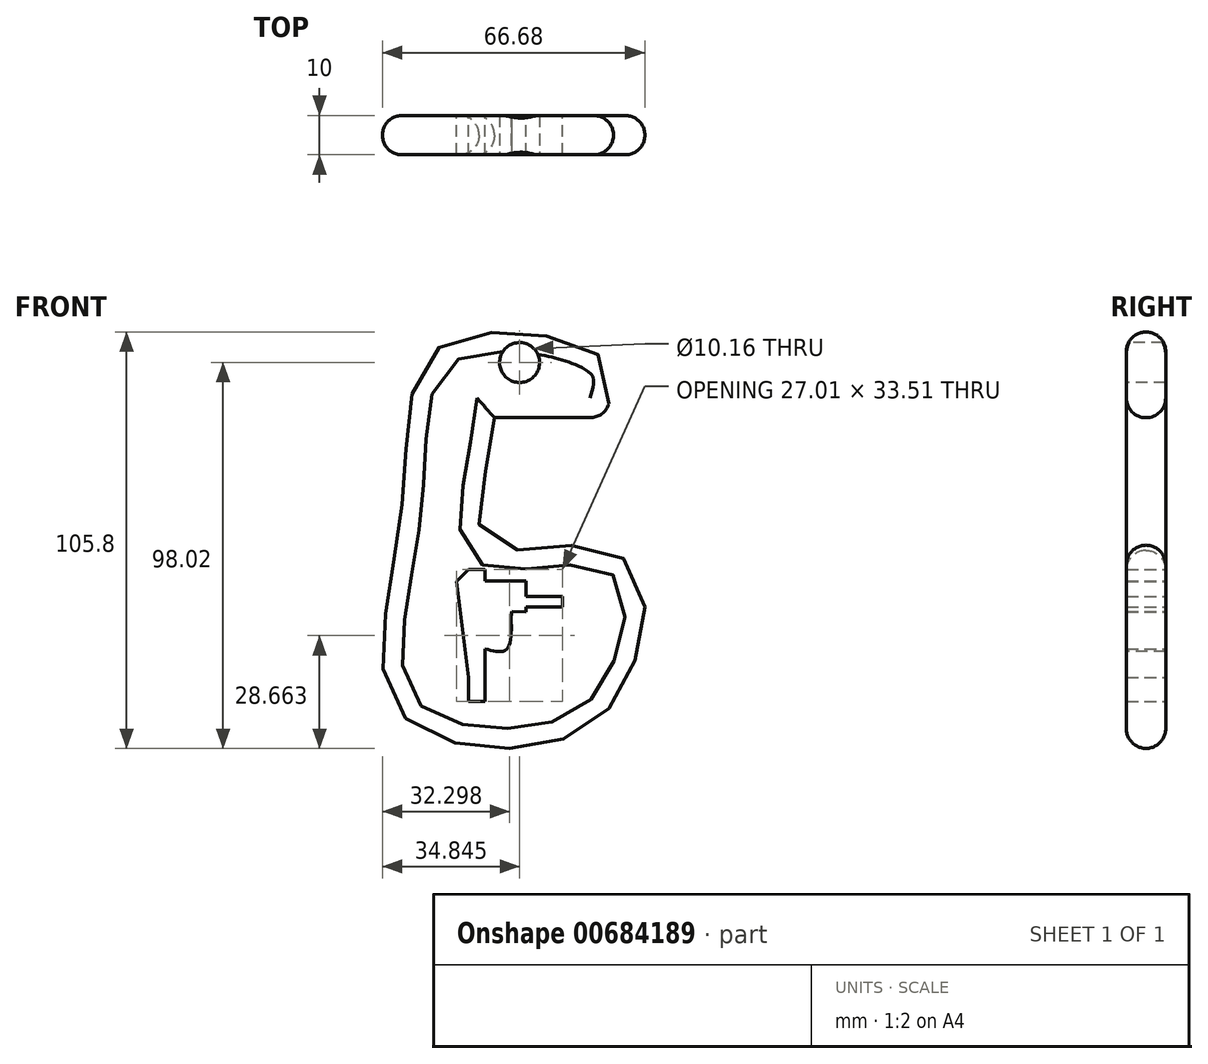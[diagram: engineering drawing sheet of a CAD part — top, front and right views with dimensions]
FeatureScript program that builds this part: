
annotation { "Feature Type Name" : "Feature", "Feature Type Description" : "" }
export const myFeature = defineFeature(function(context is Context, id is Id, definition is map)
    precondition{}
    {
        {
            var Q0;
            Q0=qCreatedBy(makeId("Front.planeOp"),FACE);
            var sketch = newSketch(context, id + "F0", { "sketchPlane" : qUnion([Q0])});
            skLineSegment(sketch, "E0", {"start": v(0, 32.39) * mm, "end": v(27.92, 32.39) * mm});
            skFitSpline(sketch, "E1", {"points": [v(27.92, 32.39) * mm, v(27.92, 47.21) * mm, v(-13.1, 50.87) * mm, v(-23.45, 9.85) * mm, v(-24.47, -41.93) * mm, v(15.74, -49.85) * mm, v(34.62, -32.19) * mm, v(36.65, -7.82) * mm, v(20.61, 0) * mm, v(-1.73, 0) * mm, v(0, 32.39) * mm], "startDerivative": vector(85.73, 266.25) * mm, "endDerivative": vector(64.37, 478.6) * mm});
            skLineSegment(sketch, "E2", {"start": v(8.02, -16.96) * mm, "end": v(8.02, -9.04) * mm});
            skLineSegment(sketch, "E3", {"start": v(8.02, -9.04) * mm, "end": v(-2.34, -9.04) * mm});
            skLineSegment(sketch, "E4", {"start": v(-2.34, -9.04) * mm, "end": v(-2.34, -6.2) * mm});
            skLineSegment(sketch, "E5", {"start": v(-2.34, -6.2) * mm, "end": v(-6.6, -6.2) * mm});
            skLineSegment(sketch, "E6", {"start": v(-6.6, -6.2) * mm, "end": v(-6.6, -39.7) * mm});
            skLineSegment(sketch, "E7", {"start": v(-6.6, -39.7) * mm, "end": v(-2.34, -39.7) * mm});
            skLineSegment(sketch, "E8", {"start": v(-2.34, -39.7) * mm, "end": v(-2.34, -16.55) * mm});
            skLineSegment(sketch, "E9", {"start": v(-2.34, -16.55) * mm, "end": v(8.02, -16.96) * mm});
            skLineSegment(sketch, "E10", {"start": v(8.02, -13) * mm, "end": v(17.36, -13) * mm});
            skLineSegment(sketch, "E11", {"start": v(17.36, -15.74) * mm, "end": v(8.02, -15.74) * mm});
            skLineSegment(sketch, "E12", {"start": v(8.02, -15.74) * mm, "end": v(17.36, -13) * mm});
            skLineSegment(sketch, "E13", {"start": v(17.36, -15.74) * mm, "end": v(17.36, -13) * mm});
            skFitSpline(sketch, "E14", {"points": [v(-2.34, -26.3) * mm, v(3.55, -25.9) * mm, v(4.42, -16.82) * mm, v(4.8, -16.83) * mm], "startDerivative": vector(18.2, -5.25) * mm, "endDerivative": vector(4.34, -2.4) * mm});
            skPoint(sketch, "E15.2.internal.snap0", {"position": v(2.84, -16.75) * mm});
            skFitSpline(sketch, "E15", {"points": [v(-2.34, -19.8) * mm, v(0, -20.2) * mm, v(0, -16.75) * mm, v(0, -16.55) * mm], "startDerivative": vector(7.32, -3.65) * mm, "endDerivative": vector(0.18, 0.9) * mm});
            skLineSegment(sketch, "E16", {"start": v(-6.6, -6.2) * mm, "end": v(-9.65, -9.24) * mm});
            skLineSegment(sketch, "E17", {"start": v(-9.65, -9.24) * mm, "end": v(-6.6, -33.6) * mm});
            skSolve(sketch);
        }
        {
            var Q0;
            Q0 = qSketchRegion(id + "F0", true);
            extrude(context, id + "F1", {"entities" : qUnion([Q0]), "depth" : 10 * mm, "offsetDistance" : 25.4 * mm});
        }
        {
            var Q0;
            Q0=makeQuery(id+"F1.opExtrude","CAP_FACE",FACE,{"disambiguationData":[OSD([sQuery(id+"F0.wireOp",EDGE,"E0"),sQuery(id+"F0.wireOp",EDGE,"E1"),sQuery(id+"F0.wireOp",EDGE,"E2"),sQuery(id+"F0.wireOp",EDGE,"E3"),sQuery(id+"F0.wireOp",EDGE,"E4"),sQuery(id+"F0.wireOp",EDGE,"E5"),sQuery(id+"F0.wireOp",EDGE,"E6"),sQuery(id+"F0.wireOp",EDGE,"E7"),sQuery(id+"F0.wireOp",EDGE,"E8"),sQuery(id+"F0.wireOp",EDGE,"E9"),sQuery(id+"F0.wireOp",EDGE,"E10"),sQuery(id+"F0.wireOp",EDGE,"E11"),sQuery(id+"F0.wireOp",EDGE,"E13"),sQuery(id+"F0.wireOp",EDGE,"E14"),sQuery(id+"F0.wireOp",EDGE,"E16"),sQuery(id+"F0.wireOp",EDGE,"E17")])],"isStart":false});
            var sketch = newSketch(context, id + "F2", { "sketchPlane" : qUnion([Q0])});
            skCircle(sketch, "E18", {"center": v(6.4, 46.4) * mm, "radius": 5.08 * mm});
            skSolve(sketch);
        }
        {
            var Q0;
            Q0=makeQuery(id+"F2.imprint","IMPRINT",FACE,{"disambiguationData":[TD([[makeQuery(id+"F2.imprint","IMPRINT",EDGE,{"derivedFrom":sQuery(id+"F2.wireOp",EDGE,"E18")}),1.0]])]});
            extrude(context, id + "F3", {"entities" : qUnion([Q0]), "operationType" : NewBodyOperationType.REMOVE, "oppositeDirection" : true, "depth" : 42.2 * mm, "offsetDistance" : 25 * mm});
        }
        {
            var Q0;
            Q0=makeQuery(id+"F1.opExtrude","CAP_EDGE",EDGE,{"disambiguationData":[OSD([sQuery(id+"F0.wireOp",EDGE,"E1")])],"isStart":false});
            var Q1;
            Q1=makeQuery(id+"F1.opExtrude","CAP_EDGE",EDGE,{"disambiguationData":[OSD([sQuery(id+"F0.wireOp",EDGE,"E0")])],"isStart":false});
            var Q2;
            {var subQ0=sQuery(id+"F0.wireOp",EDGE,"E1");var subQ1=sQuery(id+"F0.wireOp",EDGE,"E0");Q2=makeQuery(id+"F1.opExtrude","SWEPT_EDGE",EDGE,{"disambiguationData":[OSD([subQ1,subQ0]),TDD([makeQuery(id+"F0.imprint","INTERSECT",VERTEX,{"disambiguationData":[OD(1.0)],"derivedFrom":[subQ1,subQ0]})])]});}
            var Q3;
            Q3=makeQuery(id+"F1.opExtrude","CAP_EDGE",EDGE,{"disambiguationData":[OSD([sQuery(id+"F0.wireOp",EDGE,"E0")])],"isStart":true});
            var Q4;
            Q4=makeQuery(id+"F1.opExtrude","CAP_EDGE",EDGE,{"disambiguationData":[OSD([sQuery(id+"F0.wireOp",EDGE,"E1")])],"isStart":true});
            fillet(context, id + "F4", {"entities" : qUnion([Q0, Q1, Q2, Q3, Q4]), "radius" : 5 * mm, "tangentPropagation" : true, "allowEdgeOverflow" : false});
        }
        {
            var Q0;
            Q0=makeQuery(id+"F1.opExtrude","CAP_FACE",FACE,{"disambiguationData":[OSD([sQuery(id+"F0.wireOp",EDGE,"E0"),sQuery(id+"F0.wireOp",EDGE,"E1"),sQuery(id+"F0.wireOp",EDGE,"E2"),sQuery(id+"F0.wireOp",EDGE,"E3"),sQuery(id+"F0.wireOp",EDGE,"E4"),sQuery(id+"F0.wireOp",EDGE,"E5"),sQuery(id+"F0.wireOp",EDGE,"E6"),sQuery(id+"F0.wireOp",EDGE,"E7"),sQuery(id+"F0.wireOp",EDGE,"E8"),sQuery(id+"F0.wireOp",EDGE,"E9"),sQuery(id+"F0.wireOp",EDGE,"E10"),sQuery(id+"F0.wireOp",EDGE,"E11"),sQuery(id+"F0.wireOp",EDGE,"E13"),sQuery(id+"F0.wireOp",EDGE,"E14"),sQuery(id+"F0.wireOp",EDGE,"E16"),sQuery(id+"F0.wireOp",EDGE,"E17")])],"isStart":false});
            var sketch = newSketch(context, id + "F5", { "sketchPlane" : qUnion([Q0])});
            skArc(sketch, "E19", {"start": v(-60.64, -56.53) * mm, "mid": v(-27.57, -75.02) * mm, "end": v(0, -49.03) * mm});
            skLineSegment(sketch, "E20", {"start": v(-60.64, -56.53) * mm, "end": v(-60.64, 46.22) * mm});
            skSolve(sketch);
        }
    });
